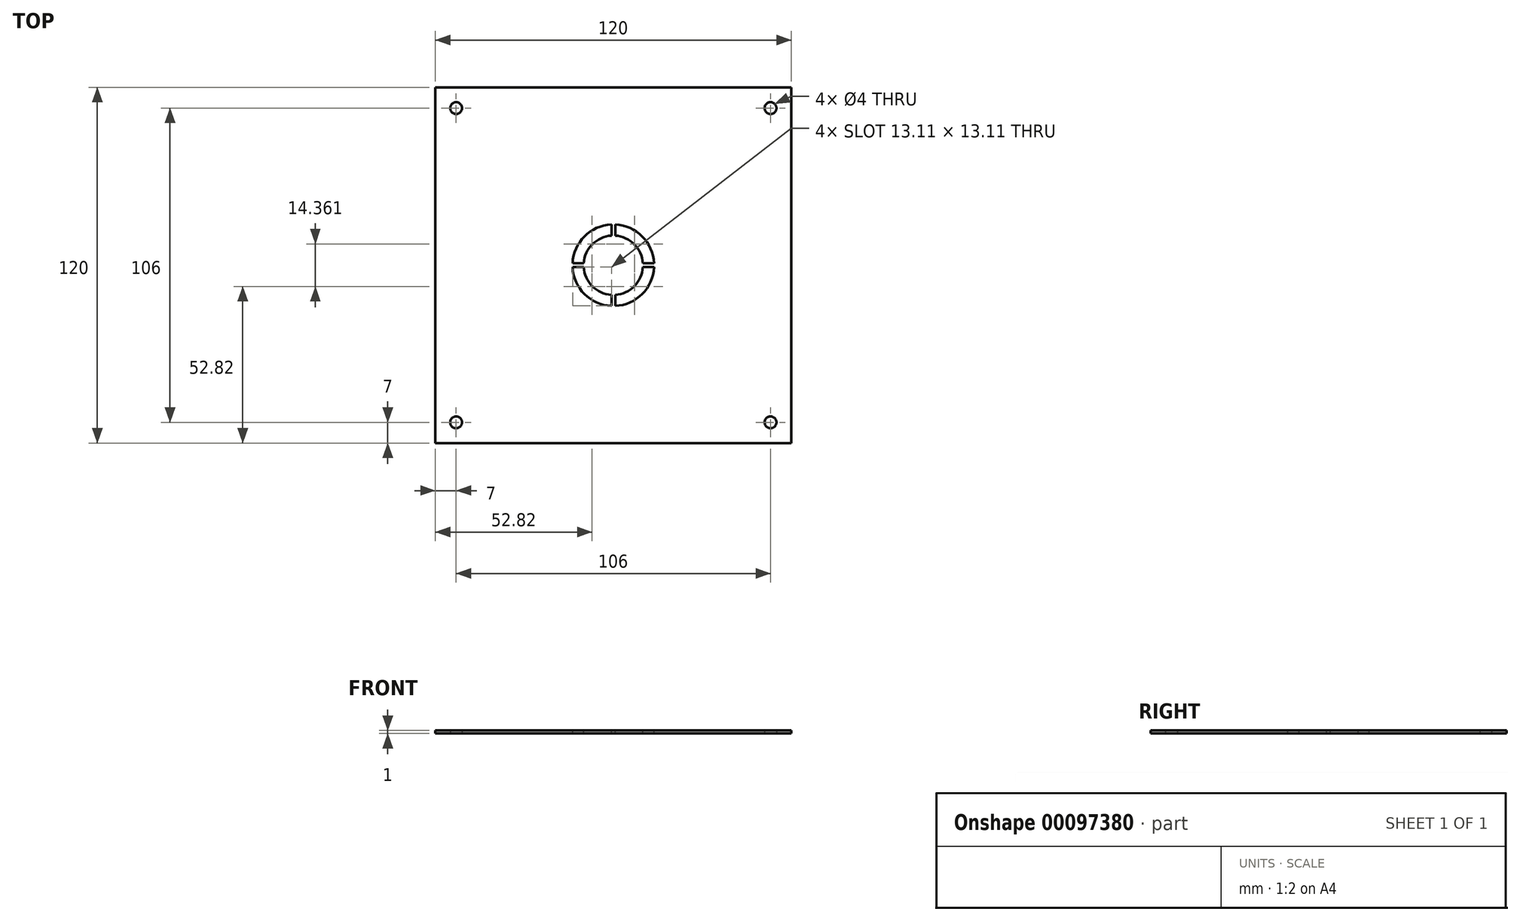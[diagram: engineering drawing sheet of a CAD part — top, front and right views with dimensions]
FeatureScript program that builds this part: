
annotation { "Feature Type Name" : "Feature", "Feature Type Description" : "" }
export const myFeature = defineFeature(function(context is Context, id is Id, definition is map)
    precondition{}
    {
        {
            assignVariable(context, id + "F0", {"name" : "inc", "anyValue" : 10});
        }
        {
            assignVariable(context, id + "F1", {"name" : "diam", "anyValue" : 10});
        }
        {
            assignVariable(context, id + "F2", {"name" : "diam", "anyValue" : getVariable(context, 'diam') + getVariable(context, 'inc')});
        }
        {
            var Q0;
            Q0=qCreatedBy(makeId("Top.planeOp"),FACE);
            var sketch = newSketch(context, id + "F3", { "sketchPlane" : qUnion([Q0])});
            skLineSegment(sketch, "E0.bottom", {"start": v(60, 60) * mm, "end": v(-60, 60) * mm});
            skLineSegment(sketch, "E0.top", {"start": v(60, -60) * mm, "end": v(-60, -60) * mm});
            skLineSegment(sketch, "E0.left", {"start": v(60, 60) * mm, "end": v(60, -60) * mm});
            skLineSegment(sketch, "E0.right", {"start": v(-60, 60) * mm, "end": v(-60, -60) * mm});
            skPoint(sketch, "E0.middle", {"position": v(0, 0) * mm});
            skCircle(sketch, "E1", {"center": v(0, 0) * mm, "radius": 60 * mm, "construction": true});
            skLineSegment(sketch, "E2", {"start": v(0, 60) * mm, "end": v(0, -60) * mm, "construction": true});
            skLineSegment(sketch, "E3", {"start": v(-60, 0) * mm, "end": v(60, 0) * mm, "construction": true});
            skLineSegment(sketch, "E4", {"start": v(-0.63, 60) * mm, "end": v(-0.62, -60) * mm});
            skLineSegment(sketch, "E5.MirrorCS", {"start": v(0.63, 60) * mm, "end": v(0.62, -60) * mm});
            skLineSegment(sketch, "E6", {"start": v(-60, 0.62) * mm, "end": v(60, 0.63) * mm});
            skLineSegment(sketch, "E7.MirrorCS", {"start": v(-60, -0.62) * mm, "end": v(60, -0.63) * mm});
            skCircle(sketch, "E8", {"center": v(-53, -53) * mm, "radius": 2 * mm});
            skCircle(sketch, "E9.MirrorC", {"center": v(-53, 53) * mm, "radius": 2 * mm});
            skCircle(sketch, "E10.MirrorC", {"center": v(53, 53) * mm, "radius": 2 * mm});
            skCircle(sketch, "E11.MirrorC", {"center": v(53, -53) * mm, "radius": 2 * mm});
            skSolve(sketch);
        }
        {
            var Q0;
            Q0 = qSketchRegion(id + "F3", true);
            var Q1;
            {var subQ0=sQuery(id+"F3.wireOp",EDGE,"E6");var subQ1=sQuery(id+"F3.wireOp",EDGE,"E4");var subQ2=makeQuery(id+"F3.imprint","INTERSECT",VERTEX,{"derivedFrom":[subQ1,subQ0]});Q1=makeQuery(id+"F3.imprint","IMPRINT",FACE,{"disambiguationData":[TD([[makeQuery(id+"F3.imprint","IMPRINT",EDGE,{"disambiguationData":[TD([[subQ2,-1.0]])],"derivedFrom":subQ1}),1.0]])]});}
            extrude(context, id + "F4", {"entities" : qUnion([Q0, Q1]), "depth" : 1 * mm});
        }
        {
            var Q0;
            Q0=makeQuery(id+"F4.opExtrude","CAP_FACE",FACE,{"disambiguationData":[OSD([sQuery(id+"F3.wireOp",EDGE,"E0.bottom"),sQuery(id+"F3.wireOp",EDGE,"E0.top"),sQuery(id+"F3.wireOp",EDGE,"E0.left"),sQuery(id+"F3.wireOp",EDGE,"E0.right")])],"isStart":false});
            var sketch = newSketch(context, id + "F5", { "sketchPlane" : qUnion([Q0])});
            skCircle(sketch, "E12", {"center": v(0, 0) * mm, "radius": 10 * mm});
            skCircle(sketch, "E13", {"center": v(0, 0) * mm, "radius": 13.75 * mm});
            skSolve(sketch);
        }
        {
            var Q0;
            Q0=makeQuery(id+"F5.imprint","IMPRINT",FACE,{"disambiguationData":[TD([[makeQuery(id+"F5.imprint","IMPRINT",EDGE,{"derivedFrom":sQuery(id+"F5.wireOp",EDGE,"E12")}),-1.0]])]});
            extrude(context, id + "F6", {"entities" : qUnion([Q0]), "operationType" : NewBodyOperationType.REMOVE, "endBound" : BoundingType.THROUGH_ALL, "oppositeDirection" : true, "depth" : 25 * mm});
        }
        {
            var Q0;
            {var subQ0=sQuery(id+"F3.wireOp",EDGE,"E6");var subQ1=sQuery(id+"F3.wireOp",EDGE,"E0.right");var subQ2=makeQuery(id+"F3.imprint","INTERSECT",VERTEX,{"derivedFrom":[subQ1,subQ0]});Q0=makeQuery(id+"F3.imprint","IMPRINT",FACE,{"disambiguationData":[TD([[makeQuery(id+"F3.imprint","IMPRINT",EDGE,{"disambiguationData":[TD([[subQ2,-1.0]])],"derivedFrom":subQ1}),1.0]])]});}
            var Q1;
            {var subQ0=sQuery(id+"F3.wireOp",EDGE,"E6");var subQ1=sQuery(id+"F3.wireOp",EDGE,"E4");var subQ2=makeQuery(id+"F3.imprint","INTERSECT",VERTEX,{"derivedFrom":[subQ1,subQ0]});Q1=makeQuery(id+"F3.imprint","IMPRINT",FACE,{"disambiguationData":[TD([[makeQuery(id+"F3.imprint","IMPRINT",EDGE,{"disambiguationData":[TD([[subQ2,-1.0]])],"derivedFrom":subQ1}),1.0]])]});}
            var Q2;
            {var subQ0=sQuery(id+"F3.wireOp",EDGE,"E4");var subQ1=sQuery(id+"F3.wireOp",EDGE,"E0.bottom");var subQ2=makeQuery(id+"F3.imprint","INTERSECT",VERTEX,{"derivedFrom":[subQ1,subQ0]});Q2=makeQuery(id+"F3.imprint","IMPRINT",FACE,{"disambiguationData":[TD([[makeQuery(id+"F3.imprint","IMPRINT",EDGE,{"disambiguationData":[TD([[subQ2,1.0]])],"derivedFrom":subQ1}),1.0]])]});}
            var Q3;
            {var subQ0=sQuery(id+"F3.wireOp",EDGE,"E6");var subQ1=sQuery(id+"F3.wireOp",EDGE,"E0.left");var subQ2=makeQuery(id+"F3.imprint","INTERSECT",VERTEX,{"derivedFrom":[subQ1,subQ0]});Q3=makeQuery(id+"F3.imprint","IMPRINT",FACE,{"disambiguationData":[TD([[makeQuery(id+"F3.imprint","IMPRINT",EDGE,{"disambiguationData":[TD([[subQ2,-1.0]])],"derivedFrom":subQ1}),-1.0]])]});}
            var Q4;
            {var subQ0=sQuery(id+"F3.wireOp",EDGE,"E4");var subQ1=sQuery(id+"F3.wireOp",EDGE,"E0.top");var subQ2=makeQuery(id+"F3.imprint","INTERSECT",VERTEX,{"derivedFrom":[subQ1,subQ0]});Q4=makeQuery(id+"F3.imprint","IMPRINT",FACE,{"disambiguationData":[TD([[makeQuery(id+"F3.imprint","IMPRINT",EDGE,{"disambiguationData":[TD([[subQ2,1.0]])],"derivedFrom":subQ1}),-1.0]])]});}
            extrude(context, id + "F7", {"entities" : qUnion([Q0, Q1, Q2, Q3, Q4]), "operationType" : NewBodyOperationType.ADD, "depth" : 1 * mm});
        }
    });
